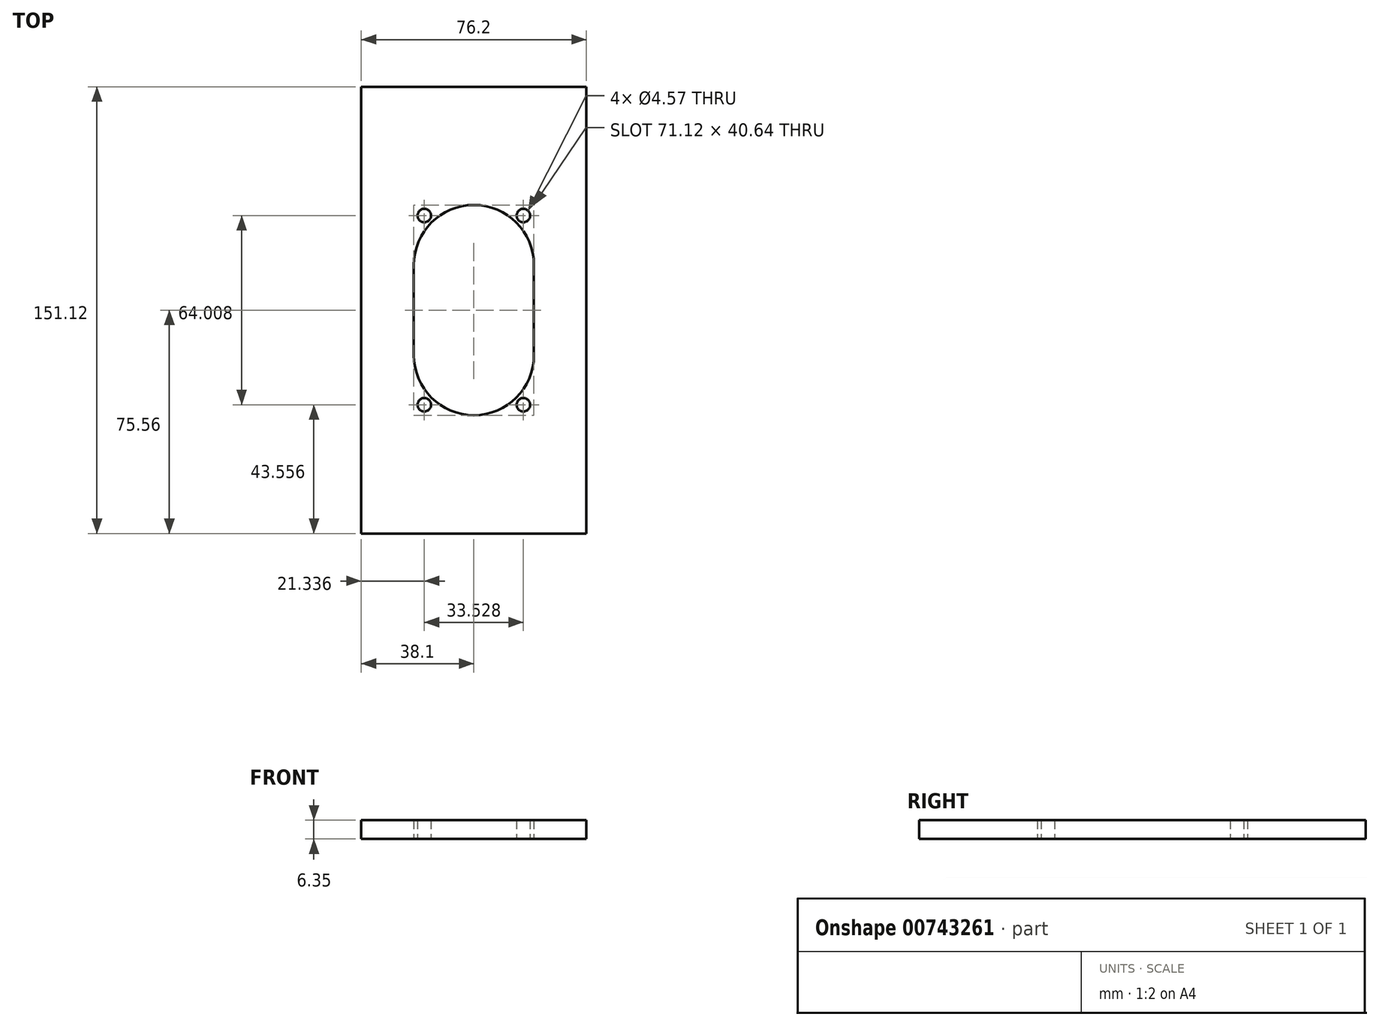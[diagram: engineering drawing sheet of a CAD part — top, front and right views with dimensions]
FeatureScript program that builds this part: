
annotation { "Feature Type Name" : "Feature", "Feature Type Description" : "" }
export const myFeature = defineFeature(function(context is Context, id is Id, definition is map)
    precondition{}
    {
        {
            var Q0;
            Q0=qCreatedBy(makeId("Top.planeOp"),FACE);
            var sketch = newSketch(context, id + "F0", { "sketchPlane" : qUnion([Q0])});
            skLineSegment(sketch, "E0.bottom", {"start": v(-38.1, 75.56) * mm, "end": v(38.1, 75.57) * mm});
            skLineSegment(sketch, "E0.top", {"start": v(-38.1, -75.57) * mm, "end": v(38.1, -75.57) * mm});
            skLineSegment(sketch, "E0.left", {"start": v(-38.1, 75.56) * mm, "end": v(-38.1, -75.56) * mm});
            skLineSegment(sketch, "E0.right", {"start": v(38.1, 75.57) * mm, "end": v(38.1, -75.57) * mm});
            skPoint(sketch, "E0.middle", {"position": v(0, 0) * mm});
            skLineSegment(sketch, "E1.bottom", {"start": v(20.32, 35.56) * mm, "end": v(-20.32, 35.56) * mm});
            skLineSegment(sketch, "E1.top", {"start": v(20.32, -35.56) * mm, "end": v(-20.32, -35.56) * mm});
            skLineSegment(sketch, "E1.left", {"start": v(20.32, 35.56) * mm, "end": v(20.32, -35.56) * mm});
            skLineSegment(sketch, "E1.right", {"start": v(-20.32, 35.56) * mm, "end": v(-20.32, -35.56) * mm});
            skPoint(sketch, "E2.first.point", {"position": v(0, -35.56) * mm});
            skCircle(sketch, "E3", {"center": v(0, -15.24) * mm, "radius": 20.32 * mm});
            skCircle(sketch, "E4", {"center": v(0, 15.24) * mm, "radius": 20.32 * mm});
            skCircle(sketch, "E5", {"center": v(-16.76, -32) * mm, "radius": 2.29 * mm});
            skCircle(sketch, "E6", {"center": v(16.76, -32) * mm, "radius": 2.29 * mm});
            skCircle(sketch, "E7", {"center": v(-16.76, 32) * mm, "radius": 2.29 * mm});
            skCircle(sketch, "E8", {"center": v(16.76, 32) * mm, "radius": 2.29 * mm});
            skSolve(sketch);
        }
        {
            var Q0;
            Q0=makeQuery(id+"F0.imprint","IMPRINT",FACE,{"disambiguationData":[TD([[makeQuery(id+"F0.imprint","IMPRINT",EDGE,{"derivedFrom":sQuery(id+"F0.wireOp",EDGE,"E0.bottom")}),-1.0]])]});
            var Q1;
            Q1=makeQuery(id+"F0.imprint","IMPRINT",FACE,{"disambiguationData":[TD([[makeQuery(id+"F0.imprint","IMPRINT",EDGE,{"derivedFrom":sQuery(id+"F0.wireOp",EDGE,"E5")}),-1.0]])]});
            var Q2;
            Q2=makeQuery(id+"F0.imprint","IMPRINT",FACE,{"disambiguationData":[TD([[makeQuery(id+"F0.imprint","IMPRINT",EDGE,{"derivedFrom":sQuery(id+"F0.wireOp",EDGE,"E6")}),-1.0]])]});
            var Q3;
            Q3=makeQuery(id+"F0.imprint","IMPRINT",FACE,{"disambiguationData":[TD([[makeQuery(id+"F0.imprint","IMPRINT",EDGE,{"derivedFrom":sQuery(id+"F0.wireOp",EDGE,"E7")}),-1.0]])]});
            var Q4;
            Q4=makeQuery(id+"F0.imprint","IMPRINT",FACE,{"disambiguationData":[TD([[makeQuery(id+"F0.imprint","IMPRINT",EDGE,{"derivedFrom":sQuery(id+"F0.wireOp",EDGE,"E8")}),-1.0]])]});
            extrude(context, id + "F1", {"entities" : qUnion([Q0, Q1, Q2, Q3, Q4]), "depth" : 6.35 * mm, "offsetDistance" : 25.4 * mm});
        }
        {
            var Q0;
            Q0=qCreatedBy(makeId("Top.planeOp"),FACE);
            cPlane(context, id + "F2", {"entities" : qUnion([Q0]), "cplaneType" : CPlaneType.OFFSET, "offset" : 2.54 * mm, "oppositeDirection" : true, "width" : 152.4 * mm, "height" : 152.4 * mm});
        }
    });
